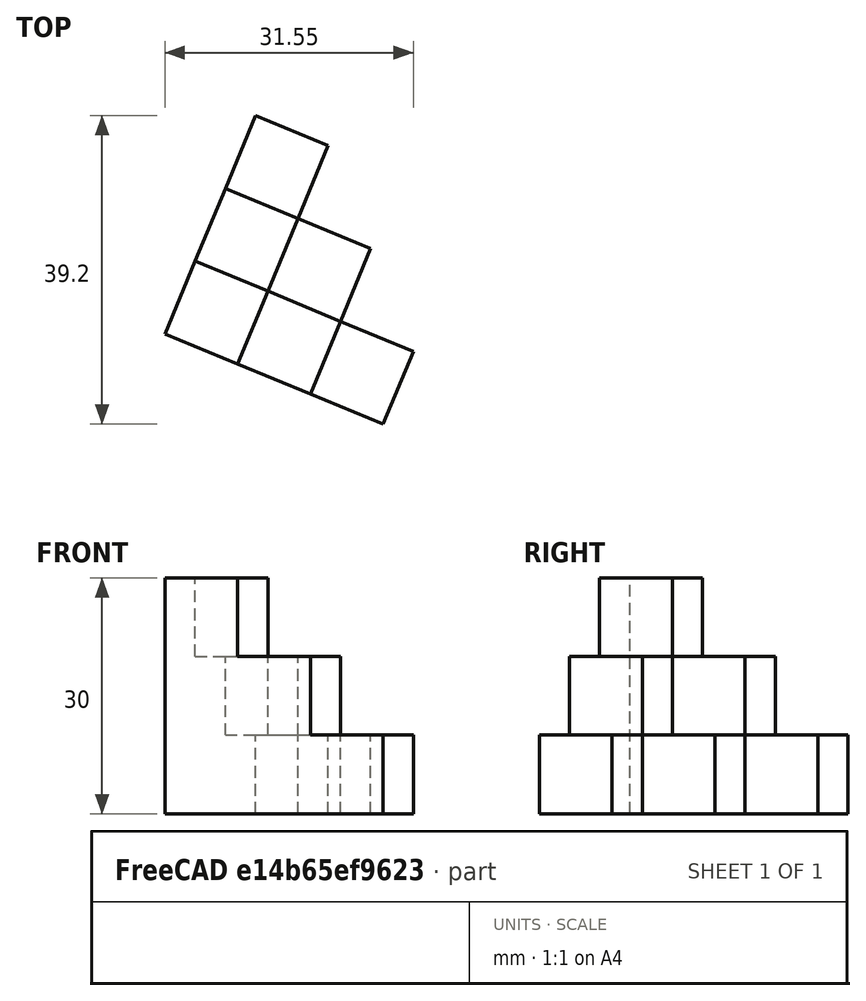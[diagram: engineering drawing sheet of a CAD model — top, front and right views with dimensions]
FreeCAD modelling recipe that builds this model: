
FCSTD DOCUMENT  (FreeCAD 0.21R33694 (Git))
Label: OJT1_TO4_P2
License: All rights reserved
LicenseURL: https://en.wikipedia.org/wiki/All_rights_reserved
objects: Part::Box×8, Part::MultiFuse×1, Part::Refine×1
note: 10 computed .brp shape members not serialized (recipe doc carries the construction recipe); baked Part::Feature solids carry a one-line shape summary decoded from their .brp

FEATURE [Part::Box] Box  label="Cub"
  AttacherType = Attacher::AttachEngine3D
  Height = 30
  Length = 10
  Width = 10
FEATURE [Part::Box] Box001  label="Cub001"
  AttacherType = Attacher::AttachEngine3D
  Height = 20
  Length = 20
  Width = 10
FEATURE [Part::Box] Box002  label="Cub002"
  AttacherType = Attacher::AttachEngine3D
  Height = 10
  Length = 10
  Width = 20
FEATURE [Part::Box] Box003  label="Cub003"
  AttacherType = Attacher::AttachEngine3D
  Height = 10
  Length = 10
  Width = 10
FEATURE [Part::Box] Box004  label="Cub004"
  AttacherType = Attacher::AttachEngine3D
  Height = 10
  Length = 30
  Width = 10
FEATURE [Part::Box] Box005  label="Cub005"
  AttacherType = Attacher::AttachEngine3D
  Height = 20
  Length = 10
  Width = 20
FEATURE [Part::Box] Box006  label="Cub006"
  AttacherType = Attacher::AttachEngine3D
  Height = 10
  Length = 10
  Width = 30
FEATURE [Part::Box] Box007  label="Cub007"
  AttacherType = Attacher::AttachEngine3D
  Height = 10
  Length = 10
  Placement = pos=(10,10,0) rot=(0,0,1;0rad)
  Width = 10
  expr: .Placement.Base.x = 10
  expr: .Placement.Base.y = 10
FEATURE [Part::MultiFuse] Fusion
  Shapes = -> [Box,Box001,Box002,Box003,Box004,Box005,Box006,Box007]
FEATURE [Part::Refine] Fusion001
  Placement = pos=(-13.8582,-5.74025,0) rot=(0,0,1;5.89049rad)
  Source = -> Fusion
